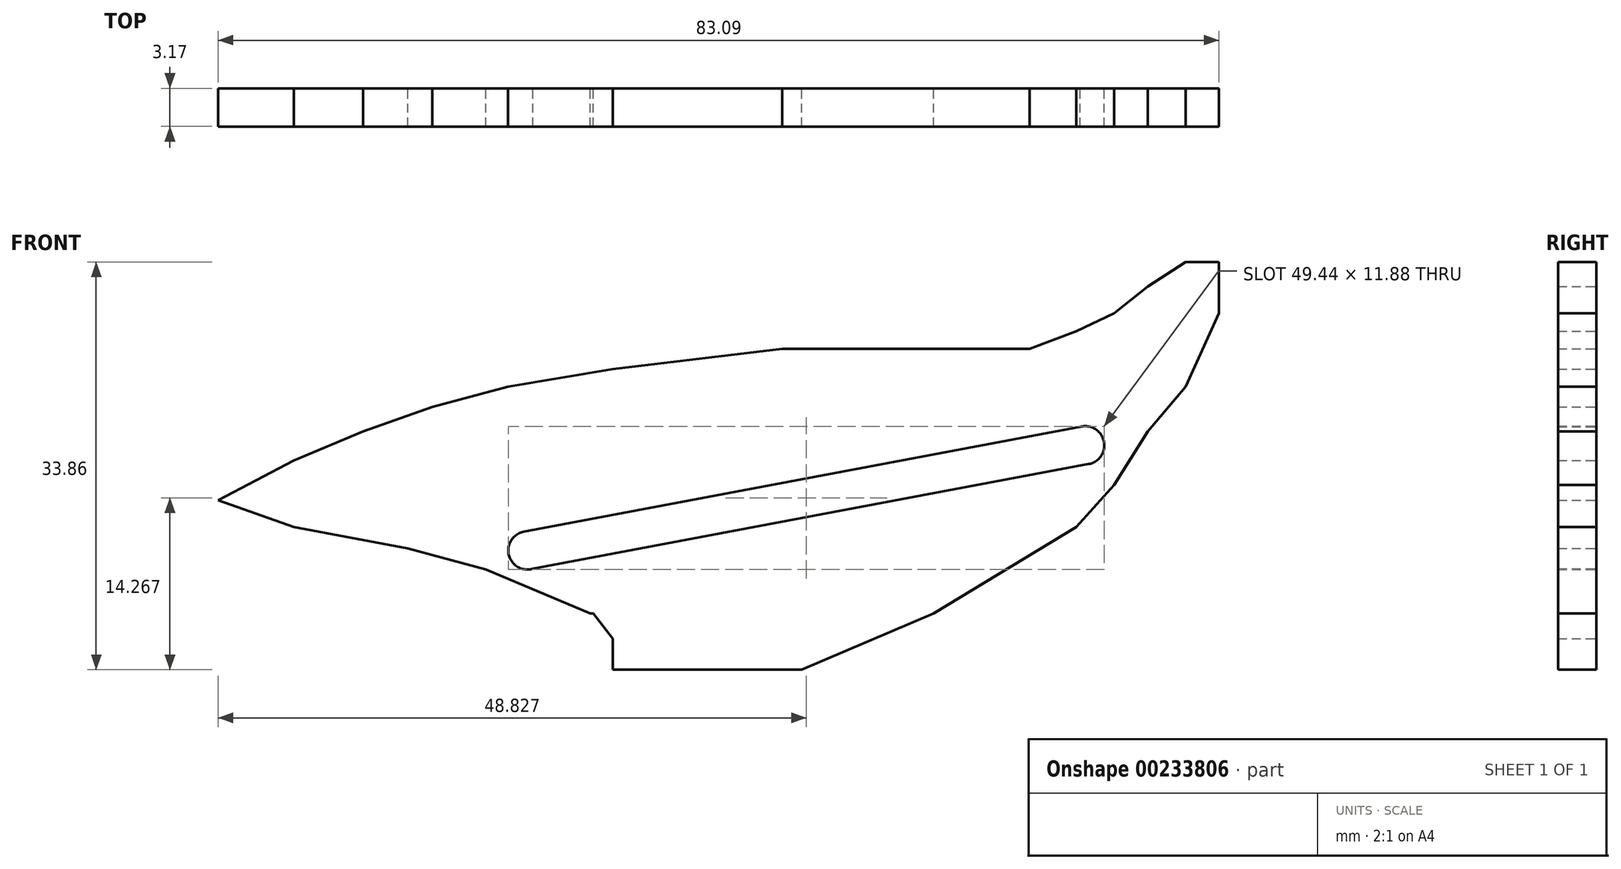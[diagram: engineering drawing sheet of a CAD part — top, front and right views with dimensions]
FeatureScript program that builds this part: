
annotation { "Feature Type Name" : "Feature", "Feature Type Description" : "" }
export const myFeature = defineFeature(function(context is Context, id is Id, definition is map)
    precondition{}
    {
        {
            var Q0;
            Q0=qCreatedBy(makeId("Front.planeOp"),FACE);
            var sketch = newSketch(context, id + "F0", { "sketchPlane" : qUnion([Q0])});
            skLineSegment(sketch, "E0", {"start": v(-48.45, 3.99) * mm, "end": v(-42.15, 7.32) * mm});
            skLineSegment(sketch, "E1", {"start": v(-42.15, 7.32) * mm, "end": v(-36.42, 9.72) * mm});
            skLineSegment(sketch, "E2", {"start": v(-36.42, 9.72) * mm, "end": v(-30.68, 11.76) * mm});
            skLineSegment(sketch, "E3", {"start": v(-30.68, 11.76) * mm, "end": v(-24.39, 13.43) * mm});
            skLineSegment(sketch, "E4", {"start": v(-24.39, 13.43) * mm, "end": v(-15.7, 14.9) * mm});
            skLineSegment(sketch, "E5", {"start": v(-15.7, 14.9) * mm, "end": v(-1.63, 16.57) * mm});
            skLineSegment(sketch, "E6", {"start": v(-1.63, 16.57) * mm, "end": v(10.95, 16.57) * mm});
            skLineSegment(sketch, "E7", {"start": v(10.95, 16.57) * mm, "end": v(18.91, 16.57) * mm});
            skLineSegment(sketch, "E8", {"start": v(18.91, 16.57) * mm, "end": v(22.8, 18.05) * mm});
            skLineSegment(sketch, "E9", {"start": v(22.8, 18.05) * mm, "end": v(25.94, 19.53) * mm});
            skLineSegment(sketch, "E10", {"start": v(25.94, 19.53) * mm, "end": v(28.72, 21.75) * mm});
            skLineSegment(sketch, "E11", {"start": v(28.72, 21.75) * mm, "end": v(31.86, 23.79) * mm});
            skLineSegment(sketch, "E12", {"start": v(31.86, 23.79) * mm, "end": v(34.64, 23.79) * mm});
            skLineSegment(sketch, "E13", {"start": v(34.64, 23.79) * mm, "end": v(34.64, 21.75) * mm});
            skLineSegment(sketch, "E14", {"start": v(34.64, 21.75) * mm, "end": v(34.64, 19.53) * mm});
            skLineSegment(sketch, "E15", {"start": v(34.64, 19.53) * mm, "end": v(31.86, 13.43) * mm});
            skLineSegment(sketch, "E16", {"start": v(31.86, 13.43) * mm, "end": v(28.72, 9.72) * mm});
            skLineSegment(sketch, "E17", {"start": v(28.72, 9.72) * mm, "end": v(25.94, 5.28) * mm});
            skLineSegment(sketch, "E18", {"start": v(25.94, 5.28) * mm, "end": v(22.8, 1.77) * mm});
            skLineSegment(sketch, "E19", {"start": v(22.8, 1.77) * mm, "end": v(10.95, -5.4) * mm});
            skLineSegment(sketch, "E20", {"start": v(10.95, -5.4) * mm, "end": v(0, -10.07) * mm});
            skLineSegment(sketch, "E21", {"start": v(0, -10.07) * mm, "end": v(-15.7, -10.07) * mm});
            skLineSegment(sketch, "E22", {"start": v(-15.7, -10.07) * mm, "end": v(-15.7, -7.48) * mm});
            skLineSegment(sketch, "E23", {"start": v(-15.7, -7.48) * mm, "end": v(-17.32, -5.4) * mm});
            skLineSegment(sketch, "E24", {"start": v(-17.32, -5.4) * mm, "end": v(-17.57, -5.4) * mm});
            skLineSegment(sketch, "E25", {"start": v(-17.57, -5.4) * mm, "end": v(-26.24, -1.75) * mm});
            skLineSegment(sketch, "E26", {"start": v(-26.24, -1.75) * mm, "end": v(-32.72, 0) * mm});
            skLineSegment(sketch, "E27", {"start": v(-32.72, 0) * mm, "end": v(-42.15, 1.77) * mm});
            skLineSegment(sketch, "E28", {"start": v(-42.15, 1.77) * mm, "end": v(-48.45, 3.99) * mm});
            skSolve(sketch);
        }
        {
            var Q0;
            Q0=makeQuery(id+"F0.imprint","IMPRINT",FACE,{"disambiguationData":[TD([[makeQuery(id+"F0.imprint","IMPRINT",EDGE,{"derivedFrom":sQuery(id+"F0.wireOp",EDGE,"E0")}),-1.0]])]});
            extrude(context, id + "F1", {"entities" : qUnion([Q0]), "depth" : 3.17 * mm});
        }
        {
            var Q0;
            Q0=qCreatedBy(makeId("Front.planeOp"),FACE);
            var sketch = newSketch(context, id + "F2", { "sketchPlane" : qUnion([Q0])});
            skLineSegment(sketch, "E29", {"start": v(-23.07, 1.4) * mm, "end": v(23.12, 10.1) * mm});
            skLineSegment(sketch, "E30", {"start": v(-22.33, -1.7) * mm, "end": v(23.83, 7) * mm});
            skArc(sketch, "E31", {"start": v(-23.07, 1.4) * mm, "mid": v(-24.32, -0.54) * mm, "end": v(-22.33, -1.7) * mm});
            skArc(sketch, "E32", {"start": v(23.83, 7) * mm, "mid": v(25.08, 8.92) * mm, "end": v(23.12, 10.1) * mm});
            skSolve(sketch);
        }
        {
            var Q0;
            Q0=qSketchRegion(id+"F2",true);
            extrude(context, id + "F3", {"entities" : qUnion([Q0]), "operationType" : NewBodyOperationType.REMOVE, "depth" : 9.14 * mm});
        }
    });
